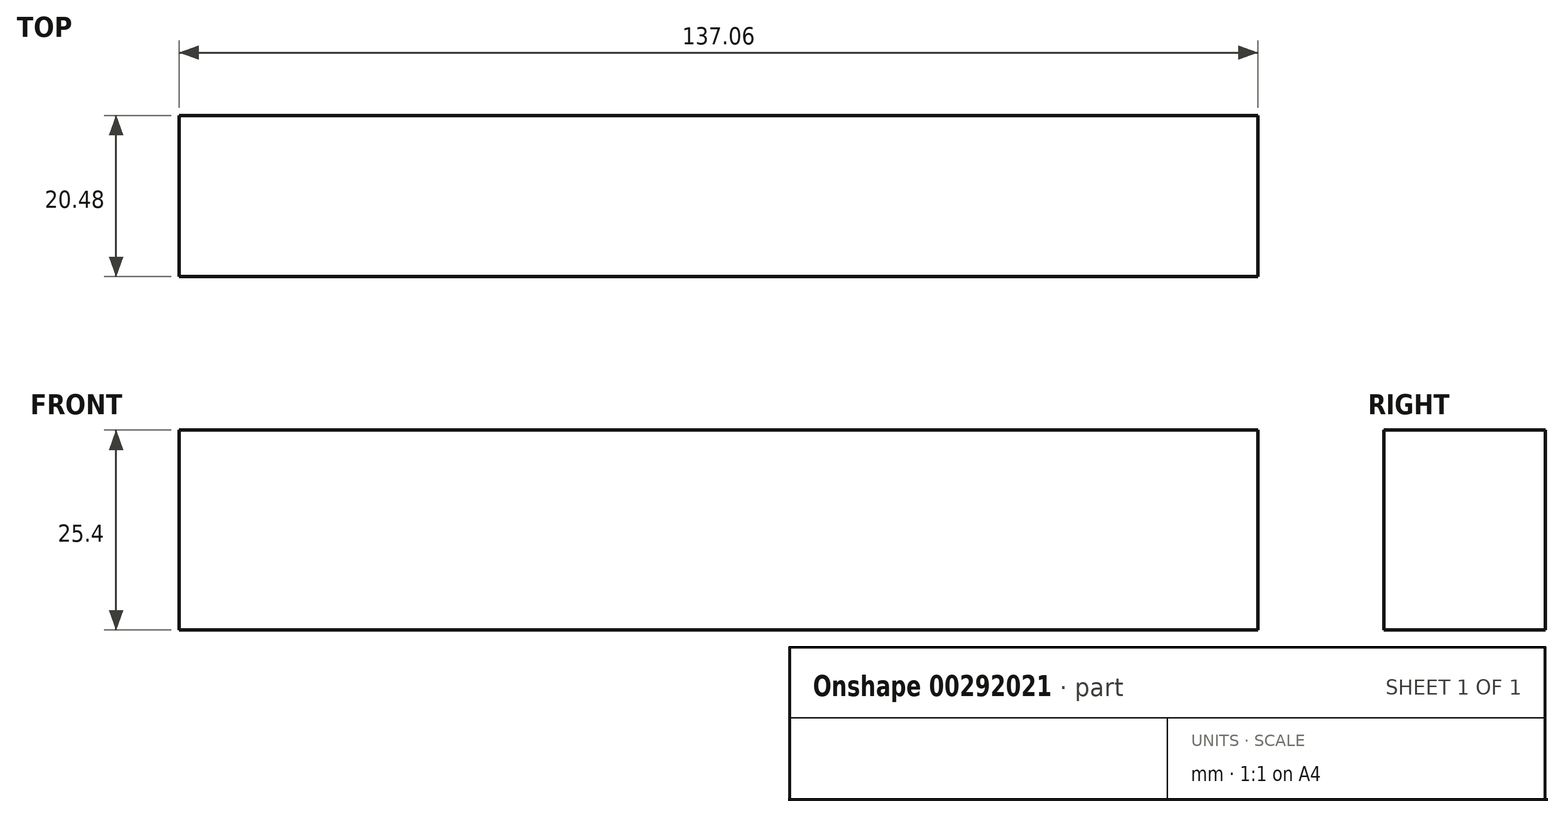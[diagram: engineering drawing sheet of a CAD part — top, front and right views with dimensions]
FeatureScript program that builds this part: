
annotation { "Feature Type Name" : "Feature", "Feature Type Description" : "" }
export const myFeature = defineFeature(function(context is Context, id is Id, definition is map)
    precondition{}
    {
        {
            var Q0;
            Q0=qCreatedBy(makeId("Top.planeOp"),FACE);
            var sketch = newSketch(context, id + "F0", { "sketchPlane" : qUnion([Q0])});
            skLineSegment(sketch, "E0.bottom", {"start": v(-95.2, 66.65) * mm, "end": v(41.87, 66.65) * mm});
            skLineSegment(sketch, "E0.top", {"start": v(-95.2, 46.17) * mm, "end": v(41.87, 46.17) * mm});
            skLineSegment(sketch, "E0.left", {"start": v(-95.2, 66.65) * mm, "end": v(-95.2, 46.17) * mm});
            skLineSegment(sketch, "E0.right", {"start": v(41.87, 66.65) * mm, "end": v(41.87, 46.17) * mm});
            skSolve(sketch);
        }
        {
            var Q0;
            Q0 = qSketchRegion(id + "F0", true);
            extrude(context, id + "F1", {"entities" : qUnion([Q0]), "depth" : 25.4 * mm});
        }
    });
